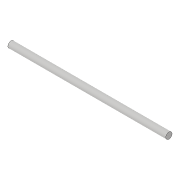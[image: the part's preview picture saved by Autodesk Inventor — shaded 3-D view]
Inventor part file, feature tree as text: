
AUTODESK INVENTOR PART (.ipt)
format: ipt  version: 2019 (Build 230136000, 136)  size: 69,120 bytes
history: native  units: in
note: dims shown in document units (in); Inventor stores cm internally (conversion verified against a paired STEP export)
features: extrude x1, sketch x1
ambient origin geometry x8: Origin, YZ Plane, XZ Plane, XY Plane, X Axis, Y Axis, Z Axis, Center Point
bodies: Solid1 (feature_tree)
feature tree (2):
  extrude  "Extrusion1"  Depth=9.8425in TaperAngle=0.0deg
  sketch  "Sketch1"  dims[d0=0.3937in d1=9.8425in d2=0.0in]
